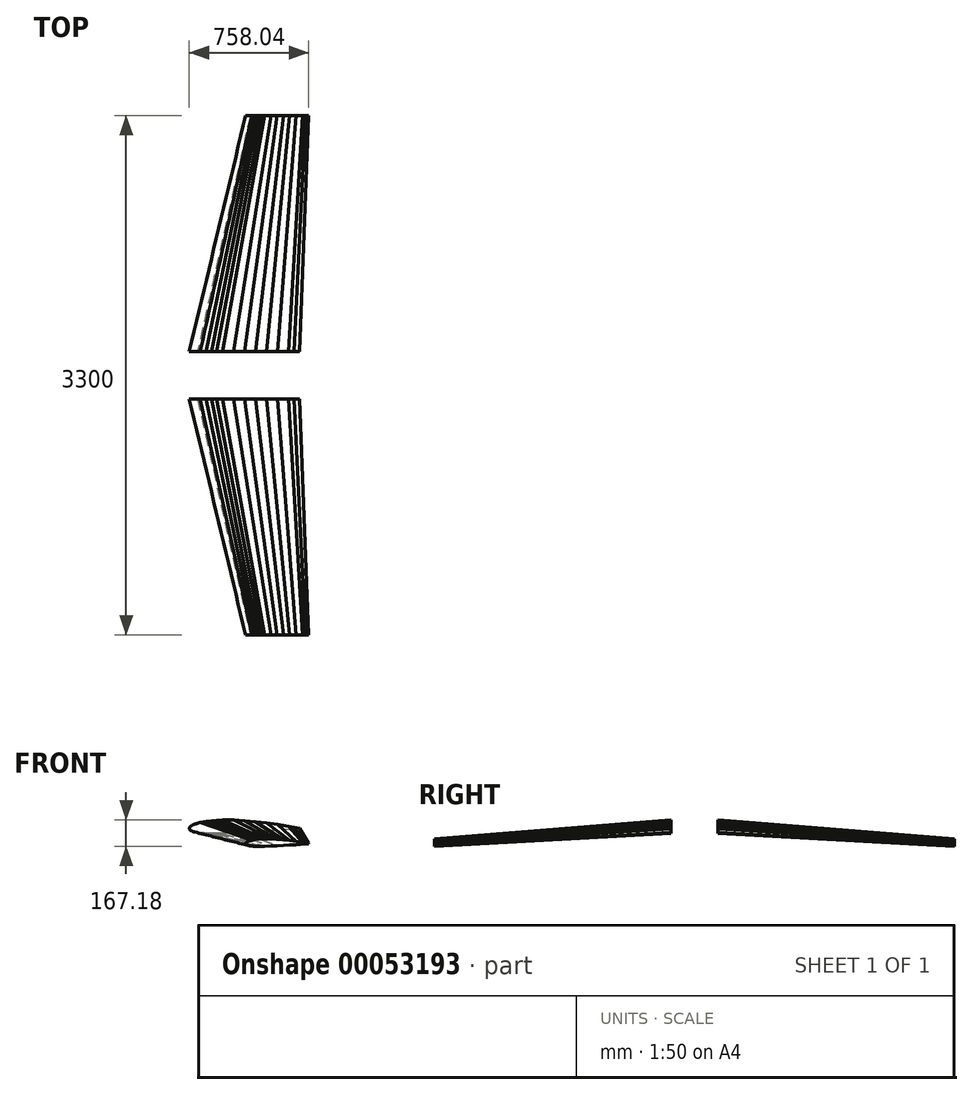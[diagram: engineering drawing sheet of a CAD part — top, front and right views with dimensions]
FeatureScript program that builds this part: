
annotation { "Feature Type Name" : "Feature", "Feature Type Description" : "" }
export const myFeature = defineFeature(function(context is Context, id is Id, definition is map)
    precondition{}
    {
        {
            var Q0;
            Q0=qCreatedBy(makeId("Front.planeOp"),FACE);
            cPlane(context, id + "F0", {"entities" : qUnion([Q0]), "cplaneType" : CPlaneType.OFFSET, "offset" : 1500 * mm, "oppositeDirection" : true, "width" : 150 * mm, "height" : 150 * mm});
        }
        {
            var Q0;
            Q0=qCreatedBy(makeId("Front.planeOp"),FACE);
            var sketch = newSketch(context, id + "F1", { "sketchPlane" : qUnion([Q0])});
            skLineSegment(sketch, "E0", {"start": v(-160, 15.22) * mm, "end": v(-140, 19.14) * mm});
            skLineSegment(sketch, "E1", {"start": v(-140, 19.14) * mm, "end": v(-120, 21.74) * mm});
            skLineSegment(sketch, "E2", {"start": v(-120, 21.74) * mm, "end": v(-100, 23.38) * mm});
            skLineSegment(sketch, "E3", {"start": v(-100, 23.38) * mm, "end": v(-80, 24.22) * mm});
            skLineSegment(sketch, "E4", {"start": v(-80, 24.22) * mm, "end": v(-40, 23.9) * mm});
            skLineSegment(sketch, "E5", {"start": v(-40, 23.9) * mm, "end": v(0, 21.66) * mm});
            skLineSegment(sketch, "E6", {"start": v(0, 21.66) * mm, "end": v(40, 18.14) * mm});
            skLineSegment(sketch, "E7", {"start": v(40, 18.14) * mm, "end": v(80, 13.42) * mm});
            skLineSegment(sketch, "E8", {"start": v(80, 13.42) * mm, "end": v(120, 7.7) * mm});
            skLineSegment(sketch, "E9", {"start": v(120, 7.7) * mm, "end": v(160, 1.02) * mm});
            skLineSegment(sketch, "E10", {"start": v(160, 1.02) * mm, "end": v(180, -2.74) * mm});
            skLineSegment(sketch, "E11", {"start": v(180, -2.74) * mm, "end": v(200, -6.78) * mm});
            skLineSegment(sketch, "E12", {"start": v(200, -6.78) * mm, "end": v(200, -7.82) * mm});
            skLineSegment(sketch, "E13", {"start": v(200, -7.82) * mm, "end": v(180, -9.22) * mm});
            skLineSegment(sketch, "E14", {"start": v(180, -9.22) * mm, "end": v(160, -10.58) * mm});
            skLineSegment(sketch, "E15", {"start": v(160, -10.58) * mm, "end": v(120, -13.3) * mm});
            skLineSegment(sketch, "E16", {"start": v(120, -13.3) * mm, "end": v(80, -15.86) * mm});
            skLineSegment(sketch, "E17", {"start": v(80, -15.86) * mm, "end": v(40, -18.34) * mm});
            skLineSegment(sketch, "E18", {"start": v(40, -18.34) * mm, "end": v(0, -20.66) * mm});
            skLineSegment(sketch, "E19", {"start": v(0, -20.66) * mm, "end": v(-40, -22.5) * mm});
            skLineSegment(sketch, "E20", {"start": v(-40, -22.5) * mm, "end": v(-80, -23.78) * mm});
            skLineSegment(sketch, "E21", {"start": v(-80, -23.78) * mm, "end": v(-100, -24.18) * mm});
            skLineSegment(sketch, "E22", {"start": v(-100, -24.18) * mm, "end": v(-120, -24.22) * mm});
            skLineSegment(sketch, "E23", {"start": v(-120, -24.22) * mm, "end": v(-140, -23.7) * mm});
            skLineSegment(sketch, "E24", {"start": v(-160, -22.3) * mm, "end": v(-170, -21.14) * mm});
            skFitSpline(sketch, "E25", {"points": [v(-160, 15.22) * mm, v(-170, 12.54) * mm, v(-180, 9.22) * mm, v(-190, 4.66) * mm, v(-195, 1.3) * mm, v(-200, -7.3) * mm, v(-195, -13.9) * mm, v(-190, -16.38) * mm, v(-180, -19.34) * mm, v(-170, -21.14) * mm, v(-160, -22.3) * mm, v(-140, -23.7) * mm], "startDerivative": vector(-108.74, -28.27) * mm, "endDerivative": vector(168.84, -10.55) * mm});
            skSolve(sketch);
        }
        {
            var Q0;
            Q0=qCreatedBy(id+"F0.planeOp",FACE);
            var sketch = newSketch(context, id + "F2", { "sketchPlane" : qUnion([Q0])});
            skLineSegment(sketch, "E26", {"start": v(-488.02, 127.21) * mm, "end": v(-453.02, 134.07) * mm});
            skLineSegment(sketch, "E27", {"start": v(-453.02, 134.07) * mm, "end": v(-418.02, 138.62) * mm});
            skLineSegment(sketch, "E28", {"start": v(-418.02, 138.62) * mm, "end": v(-383.02, 141.5) * mm});
            skLineSegment(sketch, "E29", {"start": v(-383.02, 141.5) * mm, "end": v(-348.02, 142.96) * mm});
            skLineSegment(sketch, "E30", {"start": v(-348.02, 142.96) * mm, "end": v(-278.02, 142.4) * mm});
            skLineSegment(sketch, "E31", {"start": v(-278.02, 142.4) * mm, "end": v(-208.02, 138.48) * mm});
            skLineSegment(sketch, "E32", {"start": v(-208.02, 138.48) * mm, "end": v(-138.02, 132.32) * mm});
            skLineSegment(sketch, "E33", {"start": v(-138.02, 132.32) * mm, "end": v(-68.02, 124.06) * mm});
            skLineSegment(sketch, "E34", {"start": v(-68.02, 124.06) * mm, "end": v(1.98, 114.05) * mm});
            skLineSegment(sketch, "E35", {"start": v(1.98, 114.05) * mm, "end": v(71.98, 102.36) * mm});
            skLineSegment(sketch, "E36", {"start": v(71.98, 102.36) * mm, "end": v(106.98, 95.78) * mm});
            skLineSegment(sketch, "E37", {"start": v(106.98, 95.78) * mm, "end": v(141.98, 88.71) * mm});
            skLineSegment(sketch, "E38", {"start": v(141.98, 88.71) * mm, "end": v(141.98, 86.9) * mm});
            skLineSegment(sketch, "E39", {"start": v(141.98, 86.9) * mm, "end": v(106.98, 84.44) * mm});
            skLineSegment(sketch, "E40", {"start": v(106.98, 84.44) * mm, "end": v(71.98, 82.06) * mm});
            skLineSegment(sketch, "E41", {"start": v(71.98, 82.06) * mm, "end": v(1.98, 77.3) * mm});
            skLineSegment(sketch, "E42", {"start": v(1.98, 77.3) * mm, "end": v(-68.02, 72.82) * mm});
            skLineSegment(sketch, "E43", {"start": v(-68.02, 72.82) * mm, "end": v(-138.02, 68.48) * mm});
            skLineSegment(sketch, "E44", {"start": v(-138.02, 68.48) * mm, "end": v(-208.02, 64.42) * mm});
            skLineSegment(sketch, "E45", {"start": v(-208.02, 64.42) * mm, "end": v(-278.02, 61.2) * mm});
            skLineSegment(sketch, "E46", {"start": v(-278.02, 61.2) * mm, "end": v(-348.02, 58.96) * mm});
            skLineSegment(sketch, "E47", {"start": v(-348.02, 58.96) * mm, "end": v(-383.02, 58.26) * mm});
            skLineSegment(sketch, "E48", {"start": v(-383.02, 58.26) * mm, "end": v(-418.02, 58.2) * mm});
            skLineSegment(sketch, "E49", {"start": v(-418.02, 58.2) * mm, "end": v(-453.02, 59.1) * mm});
            skLineSegment(sketch, "E50", {"start": v(-488.02, 61.55) * mm, "end": v(-505.52, 63.58) * mm});
            skFitSpline(sketch, "E51", {"points": [v(-488.02, 127.21) * mm, v(-505.52, 122.52) * mm, v(-523.02, 116.71) * mm, v(-540.52, 108.73) * mm, v(-549.27, 102.85) * mm, v(-558.02, 87.8) * mm, v(-549.27, 76.25) * mm, v(-540.52, 71.91) * mm, v(-523.02, 66.73) * mm, v(-505.52, 63.58) * mm, v(-488.02, 61.55) * mm, v(-453.02, 59.1) * mm], "startDerivative": vector(-566.1, -151.71) * mm, "endDerivative": vector(295.46, -18.47) * mm});
            skFitSpline(sketch, "E52", {"points": [v(71.98, 102.36) * mm, v(1.98, 114.05) * mm, v(-68.02, 124.06) * mm, v(-138.02, 132.32) * mm, v(-208.02, 138.48) * mm, v(-278.02, 142.4) * mm, v(-348.02, 142.96) * mm, v(-383.02, 141.5) * mm, v(-418.02, 138.62) * mm, v(-453.02, 134.07) * mm, v(-488.02, 127.21) * mm], "startDerivative": vector(-615.47, 105.94) * mm, "endDerivative": vector(-389.5, -76.34) * mm, "construction": true});
            skSolve(sketch);
        }
        {
            var Q0;
            {var subQ0=sQuery(id+"F2.wireOp",EDGE,"E26");Q0=makeQuery(id+"F2.imprint","IMPRINT",FACE,{"disambiguationData":[TD([[makeQuery(id+"F2.imprint","IMPRINT",EDGE,{"derivedFrom":subQ0}),-1.0]])]});}
            var Q1;
            {var subQ0=sQuery(id+"F1.wireOp",EDGE,"E0");Q1=makeQuery(id+"F1.imprint","IMPRINT",FACE,{"disambiguationData":[TD([[makeQuery(id+"F1.imprint","IMPRINT",EDGE,{"derivedFrom":subQ0}),-1.0]])]});}
            loft(context, id + "F3", {"sheetProfilesArray" : [{ "sheetProfileEntities" : qUnion([Q0]) }, { "sheetProfileEntities" : qUnion([Q1]) }]});
        }
        {
            var Q0;
            Q0=qCreatedBy(id+"F0.planeOp",FACE);
            cPlane(context, id + "F4", {"entities" : qUnion([Q0]), "cplaneType" : CPlaneType.OFFSET, "offset" : 150 * mm, "oppositeDirection" : true, "width" : 150 * mm, "height" : 150 * mm});
        }
        {
            var Q0;
            {var subQ0=sQuery(id+"F2.wireOp",EDGE,"E26");var subQ4=sQuery(id+"F1.wireOp",EDGE,"E0");Q0=makeQuery(id+"F3.opLoft","SWEPT_BODY",BODY,{"disambiguationData":[OSD([makeQuery(id+"F1.imprint","IMPRINT",FACE,{"disambiguationData":[TD([[makeQuery(id+"F1.imprint","IMPRINT",EDGE,{"derivedFrom":subQ4}),-1.0]])]}),makeQuery(id+"F2.imprint","IMPRINT",FACE,{"disambiguationData":[TD([[makeQuery(id+"F2.imprint","IMPRINT",EDGE,{"derivedFrom":subQ0}),-1.0]])]})])]});}
            var Q1;
            {var subQ0=sQuery(id+"F2.wireOp",EDGE,"E26");var subQ4=sQuery(id+"F1.wireOp",EDGE,"E0");Q1=makeQuery(id+"F3.opLoft","SWEPT_BODY",BODY,{"disambiguationData":[OSD([makeQuery(id+"F1.imprint","IMPRINT",FACE,{"disambiguationData":[TD([[makeQuery(id+"F1.imprint","IMPRINT",EDGE,{"derivedFrom":subQ4}),-1.0]])]}),makeQuery(id+"F2.imprint","IMPRINT",FACE,{"disambiguationData":[TD([[makeQuery(id+"F2.imprint","IMPRINT",EDGE,{"derivedFrom":subQ0}),-1.0]])]})])]});}
            var Q2;
            {var subQ0=sQuery(id+"F2.wireOp",EDGE,"E26");var subQ4=sQuery(id+"F1.wireOp",EDGE,"E0");Q2=makeQuery(id+"F3.opLoft","SWEPT_BODY",BODY,{"disambiguationData":[OSD([makeQuery(id+"F1.imprint","IMPRINT",FACE,{"disambiguationData":[TD([[makeQuery(id+"F1.imprint","IMPRINT",EDGE,{"derivedFrom":subQ4}),-1.0]])]}),makeQuery(id+"F2.imprint","IMPRINT",FACE,{"disambiguationData":[TD([[makeQuery(id+"F2.imprint","IMPRINT",EDGE,{"derivedFrom":subQ0}),-1.0]])]})])]});}
            var Q3;
            Q3=qCreatedBy(id+"F4.planeOp",FACE);
            var Q4;
            Q4=qCreatedBy(id+"F4.planeOp",FACE);
            var Q5;
            Q5=qCreatedBy(id+"F4.planeOp",FACE);
            mirror(context, id + "F5", {"entities" : qUnion([Q0, Q1, Q2]), "mirrorPlane" : qUnion([Q3, Q4, Q5])});
        }
    });
